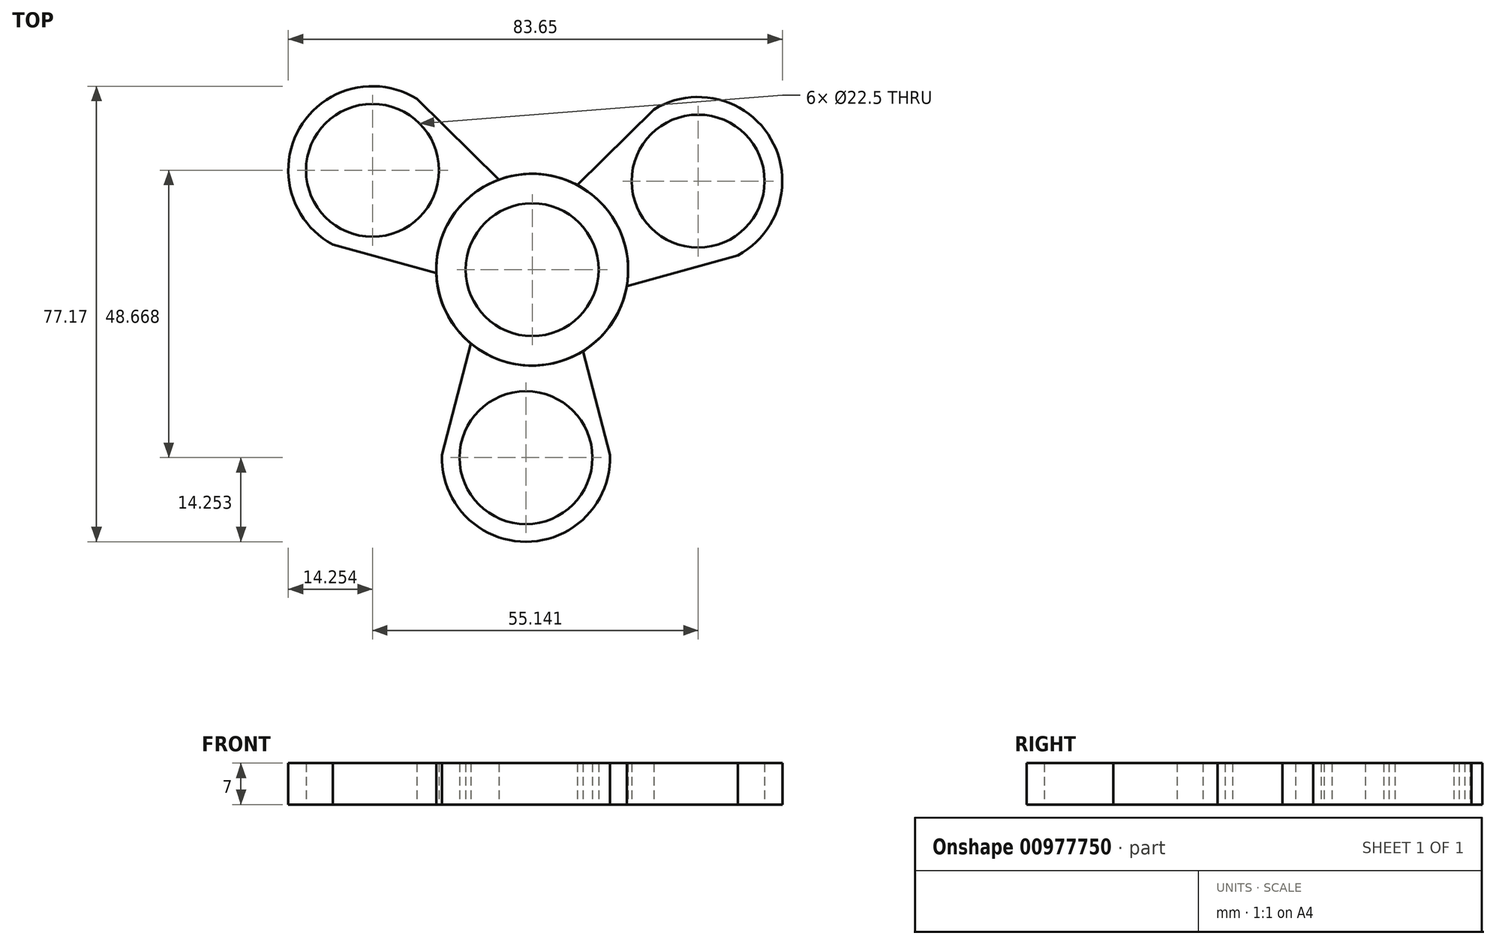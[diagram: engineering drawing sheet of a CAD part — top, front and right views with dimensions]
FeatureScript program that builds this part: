
annotation { "Feature Type Name" : "Feature", "Feature Type Description" : "" }
export const myFeature = defineFeature(function(context is Context, id is Id, definition is map)
    precondition{}
    {
        {
            var Q0;
            Q0=qCreatedBy(makeId("Top.planeOp"),FACE);
            var sketch = newSketch(context, id + "F0", { "sketchPlane" : qUnion([Q0])});
            skCircle(sketch, "E0", {"center": v(-36.4, 12.03) * mm, "radius": 11.25 * mm});
            skCircle(sketch, "E1", {"center": v(-36.4, 12.03) * mm, "radius": 16.25 * mm});
            skLineSegment(sketch, "E2", {"start": v(-37.43, -4.19) * mm, "end": v(-37.43, -4.19) * mm});
            skSolve(sketch);
        }
        {
            var Q0;
            Q0=makeQuery(id+"F0.imprint","IMPRINT",FACE,{"disambiguationData":[TD([[makeQuery(id+"F0.imprint","IMPRINT",EDGE,{"derivedFrom":sQuery(id+"F0.wireOp",EDGE,"E0")}),-1.0]])]});
            var sketch = newSketch(context, id + "F1", { "sketchPlane" : qUnion([Q0])});
            skCircle(sketch, "E3", {"center": v(-37.46, -19.8) * mm, "radius": 11.25 * mm});
            skCircle(sketch, "E4", {"center": v(-37.46, -19.8) * mm, "radius": 14.25 * mm});
            skLineSegment(sketch, "E5", {"start": v(-51.7, -19.36) * mm, "end": v(-46.69, 0) * mm});
            skLineSegment(sketch, "E6", {"start": v(-37.46, -19.8) * mm, "end": v(-37.46, -4.08) * mm, "construction": true});
            skLineSegment(sketch, "E7.MirrorCS", {"start": v(-23.22, -19.36) * mm, "end": v(-28.23, 0) * mm});
            skSolve(sketch);
        }
        {
            var Q0;
            Q0=makeQuery(id+"F0.imprint","IMPRINT",FACE,{"disambiguationData":[TD([[makeQuery(id+"F0.imprint","IMPRINT",EDGE,{"derivedFrom":sQuery(id+"F0.wireOp",EDGE,"E0")}),-1.0]])]});
            extrude(context, id + "F2", {"entities" : qUnion([Q0]), "depth" : 7 * mm, "offsetDistance" : 25 * mm});
        }
        {
            var Q0;
            {var subQ1=sQuery(id+"F1.wireOp",EDGE,"GgfPhHYs-cpLT-L7cM-Pu0L-vyKXdegyj6PM");var subQ3=makeQuery(id+"F0.imprint","IMPRINT",EDGE,{"derivedFrom":sQuery(id+"F0.wireOp",EDGE,"E1")});var subQ4=makeQuery(id+"F1.imprint","INTERSECT",VERTEX,{"disambiguationData":[OD(0.0)],"derivedFrom":[subQ3,subQ1]});Q0=makeQuery(id+"F1.imprint","IMPRINT",FACE,{"disambiguationData":[TD([[makeQuery(id+"F1.imprint","IMPRINT",EDGE,{"disambiguationData":[TD([[subQ4,1.0]])],"derivedFrom":subQ3}),-1.0]])]});}
            var Q1;
            {var subQ0=sQuery(id+"F1.wireOp",EDGE,"yMe2QiT4-c7H8-KdSz-unEN-pAifeHpbLRwF");var subQ3=makeQuery(id+"F0.imprint","IMPRINT",EDGE,{"derivedFrom":sQuery(id+"F0.wireOp",EDGE,"E1")});var subQ5=makeQuery(id+"F1.imprint","INTERSECT",VERTEX,{"derivedFrom":[subQ3,subQ0]});Q1=makeQuery(id+"F1.imprint","IMPRINT",FACE,{"disambiguationData":[TD([[makeQuery(id+"F1.imprint","IMPRINT",EDGE,{"disambiguationData":[TD([[subQ5,1.0]])],"derivedFrom":subQ3}),-1.0]])]});}
            var Q2;
            {var subQ1=sQuery(id+"F1.wireOp",EDGE,"LFMCBBJa-HOTT-z0Nd-k5nr-RxPmtrX8VNT8");Q2=makeQuery(id+"F1.imprint","IMPRINT",FACE,{"disambiguationData":[TD([[makeQuery(id+"F1.imprint","IMPRINT",EDGE,{"derivedFrom":subQ1}),1.0]])]});}
            var Q3;
            {var subQ0=sQuery(id+"F1.wireOp",EDGE,"d005a902-0fd5-438b-ba40-8045f3393e1b0.MirrorCS");Q3=makeQuery(id+"F1.imprint","IMPRINT",FACE,{"disambiguationData":[TD([[makeQuery(id+"F1.imprint","IMPRINT",EDGE,{"derivedFrom":subQ0}),-1.0]])]});}
            var Q4;
            {var subQ0=sQuery(id+"F1.wireOp",EDGE,"9xQVRCgf-rOOS-3hJd-4m8K-hfXpmJbKXl06");Q4=makeQuery(id+"F1.imprint","IMPRINT",FACE,{"disambiguationData":[TD([[makeQuery(id+"F1.imprint","IMPRINT",EDGE,{"derivedFrom":subQ0}),1.0]])]});}
            var Q5;
            Q5=makeQuery(id+"F1.imprint","IMPRINT",FACE,{"disambiguationData":[TD([[makeQuery(id+"F1.imprint","IMPRINT",EDGE,{"derivedFrom":sQuery(id+"F1.wireOp",EDGE,"E3")}),-1.0]])]});
            var Q6;
            {var subQ0=sQuery(id+"F1.wireOp",EDGE,"E4");var subQ1=sQuery(id+"F1.wireOp",EDGE,"62Sl2dqa-tp6U-FAy3-TEYR-kKC63IecdxW0");var subQ2=makeQuery(id+"F1.imprint","INTERSECT",VERTEX,{"disambiguationData":[OD(0.0)],"derivedFrom":[subQ1,subQ0]});Q6=makeQuery(id+"F1.imprint","IMPRINT",FACE,{"disambiguationData":[TD([[makeQuery(id+"F1.imprint","IMPRINT",EDGE,{"disambiguationData":[TD([[subQ2,-1.0]])],"derivedFrom":subQ1}),1.0]])]});}
            extrude(context, id + "F3", {"entities" : qUnion([Q0, Q1, Q2, Q3, Q4, Q5, Q6]), "operationType" : NewBodyOperationType.ADD, "depth" : 7 * mm, "offsetDistance" : 25 * mm});
        }
        {
            var Q0;
            Q0=makeQuery(id+"F2.opExtrude","SWEPT_BODY",BODY,{"disambiguationData":[OSD([sQuery(id+"F0.wireOp",EDGE,"E0"),sQuery(id+"F0.wireOp",EDGE,"E1")])]});
            var Q1;
            Q1=sQuery(id+"F0.wireOp",EDGE,"E1");
            circularPattern(context, id + "F4", {"entities" : qUnion([Q0]), "axis" : qUnion([Q1]), "angle" : 360 * degree, "instanceCount" : 3, "equalSpace" : true});
        }
    });
